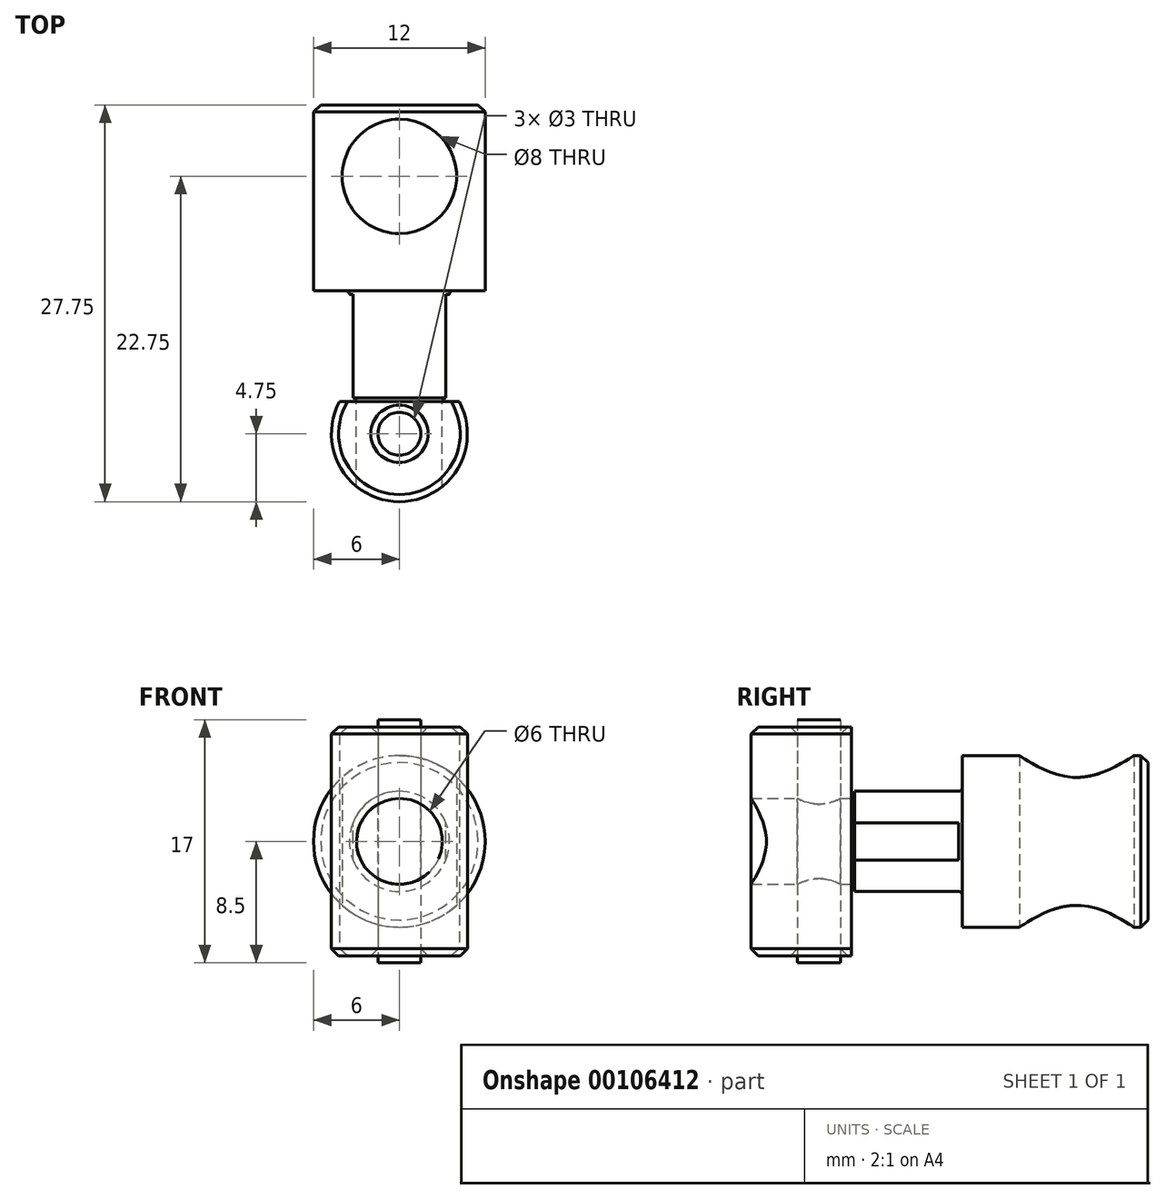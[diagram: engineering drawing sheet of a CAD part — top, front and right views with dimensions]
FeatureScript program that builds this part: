
annotation { "Feature Type Name" : "Feature", "Feature Type Description" : "" }
export const myFeature = defineFeature(function(context is Context, id is Id, definition is map)
    precondition{}
    {
        {
            var Q0;
            Q0=qCreatedBy(makeId("Top.planeOp"),FACE);
            var sketch = newSketch(context, id + "F0", { "sketchPlane" : qUnion([Q0])});
            skCircle(sketch, "E0", {"center": v(0, 0) * mm, "radius": 4.75 * mm});
            skLineSegment(sketch, "E1", {"start": v(-4.18, 2.25) * mm, "end": v(4.18, 2.25) * mm});
            skCircle(sketch, "E2", {"center": v(0, 0) * mm, "radius": 1.5 * mm});
            skSolve(sketch);
        }
        {
            var Q0;
            {var subQ0=sQuery(id+"F0.wireOp",EDGE,"E1");Q0=makeQuery(id+"F0.imprint","IMPRINT",FACE,{"disambiguationData":[TD([[makeQuery(id+"F0.imprint","IMPRINT",EDGE,{"derivedFrom":subQ0}),-1.0]])]});}
            extrude(context, id + "F1", {"entities" : qUnion([Q0]), "depth" : 16 * mm, "symmetric" : true});
        }
        {
            var Q0;
            Q0=makeQuery(id+"F1.opExtrude","CAP_EDGE",EDGE,{"disambiguationData":[OSD([sQuery(id+"F0.wireOp",EDGE,"E0")])],"isStart":false});
            var Q1;
            Q1=makeQuery(id+"F1.opExtrude","CAP_EDGE",EDGE,{"disambiguationData":[OSD([sQuery(id+"F0.wireOp",EDGE,"E0")])],"isStart":true});
            chamfer(context, id + "F2", {"entities" : qUnion([Q0, Q1]), "width" : 0.5 * mm, "tangentPropagation" : true});
        }
        {
            var Q0;
            Q0=makeQuery(id+"F1.opExtrude","SWEPT_FACE",FACE,{"disambiguationData":[OSD([sQuery(id+"F0.wireOp",EDGE,"E1")])]});
            var sketch = newSketch(context, id + "F3", { "sketchPlane" : qUnion([Q0])});
            skCircle(sketch, "E3", {"center": v(0, 0) * mm, "radius": 3 * mm});
            skSolve(sketch);
        }
        {
            var Q0;
            Q0=makeQuery(id+"F3.imprint","IMPRINT",FACE,{"disambiguationData":[TD([[makeQuery(id+"F3.imprint","IMPRINT",EDGE,{"derivedFrom":sQuery(id+"F3.wireOp",EDGE,"E3")}),1.0]])]});
            extrude(context, id + "F4", {"entities" : qUnion([Q0]), "operationType" : NewBodyOperationType.REMOVE, "endBound" : BoundingType.THROUGH_ALL, "oppositeDirection" : true, "depth" : 25 * mm});
        }
        {
            var Q0;
            Q0=qCreatedBy(makeId("Right.planeOp"),FACE);
            var sketch = newSketch(context, id + "F5", { "sketchPlane" : qUnion([Q0])});
            skLineSegment(sketch, "E4", {"start": v(-5, 0) * mm, "end": v(-5, 3) * mm});
            skLineSegment(sketch, "E5", {"start": v(-5, 3) * mm, "end": v(2.25, 3) * mm});
            skLineSegment(sketch, "E6", {"start": v(2.5, 3.25) * mm, "end": v(2.5, 3.5) * mm});
            skLineSegment(sketch, "E7", {"start": v(2.5, 3.5) * mm, "end": v(9.75, 3.5) * mm});
            skLineSegment(sketch, "E8", {"start": v(10, 3.75) * mm, "end": v(10, 6) * mm});
            skLineSegment(sketch, "E9", {"start": v(10, 6) * mm, "end": v(23, 6) * mm});
            skLineSegment(sketch, "E10", {"start": v(23, 6) * mm, "end": v(23, 0) * mm});
            skLineSegment(sketch, "E11", {"start": v(23, 0) * mm, "end": v(-5, 0) * mm});
            skPoint(sketch, "E12.visualSharp", {"position": v(2.5, 3) * mm});
            skArc(sketch, "E12.filletArc", {"start": v(2.25, 3) * mm, "mid": v(2.43, 3.07) * mm, "end": v(2.5, 3.25) * mm});
            skPoint(sketch, "E13.visualSharp", {"position": v(10, 3.5) * mm});
            skArc(sketch, "E13.filletArc", {"start": v(9.75, 3.5) * mm, "mid": v(9.93, 3.57) * mm, "end": v(10, 3.75) * mm});
            skSolve(sketch);
        }
        {
            var Q0;
            Q0=qSketchRegion(id+"F5",true);
            var Q1;
            Q1=sQuery(id+"F5.wireOp",EDGE,"E11");
            revolve(context, id + "F6", {"entities" : qUnion([Q0]), "axis" : qUnion([Q1]), "revolveType" : RevolveType.FULL});
        }
        {
            var Q0;
            Q0=qCreatedBy(makeId("Top.planeOp"),FACE);
            var sketch = newSketch(context, id + "F7", { "sketchPlane" : qUnion([Q0])});
            skLineSegment(sketch, "E14.bottom", {"start": v(-7.5, 9.75) * mm, "end": v(-3.25, 9.75) * mm});
            skLineSegment(sketch, "E14.top", {"start": v(-7.5, 2.5) * mm, "end": v(-3.25, 2.5) * mm});
            skLineSegment(sketch, "E14.left", {"start": v(-7.5, 9.75) * mm, "end": v(-7.5, 2.5) * mm});
            skLineSegment(sketch, "E14.right", {"start": v(-3.25, 9.75) * mm, "end": v(-3.25, 2.5) * mm});
            skLineSegment(sketch, "E15.bottom", {"start": v(7.5, 9.75) * mm, "end": v(3.25, 9.75) * mm});
            skLineSegment(sketch, "E15.top", {"start": v(7.5, 2.5) * mm, "end": v(3.25, 2.5) * mm});
            skLineSegment(sketch, "E15.left", {"start": v(7.5, 9.75) * mm, "end": v(7.5, 2.5) * mm});
            skLineSegment(sketch, "E15.right", {"start": v(3.25, 9.75) * mm, "end": v(3.25, 2.5) * mm});
            skSolve(sketch);
        }
        {
            var Q0;
            Q0=makeQuery(id+"F7.imprint","IMPRINT",FACE,{"disambiguationData":[TD([[makeQuery(id+"F7.imprint","IMPRINT",EDGE,{"derivedFrom":sQuery(id+"F7.wireOp",EDGE,"E14.bottom")}),-1.0]])]});
            var Q1;
            Q1=makeQuery(id+"F7.imprint","IMPRINT",FACE,{"disambiguationData":[TD([[makeQuery(id+"F7.imprint","IMPRINT",EDGE,{"derivedFrom":sQuery(id+"F7.wireOp",EDGE,"E15.bottom")}),1.0]])]});
            extrude(context, id + "F8", {"entities" : qUnion([Q0, Q1]), "operationType" : NewBodyOperationType.REMOVE, "oppositeDirection" : true, "depth" : 25 * mm, "symmetric" : true});
        }
        {
            var Q0;
            Q0=qCreatedBy(makeId("Top.planeOp"),FACE);
            var sketch = newSketch(context, id + "F9", { "sketchPlane" : qUnion([Q0])});
            skCircle(sketch, "E16", {"center": v(0, 0) * mm, "radius": 1.5 * mm});
            skSolve(sketch);
        }
        {
            var Q0;
            Q0=makeQuery(id+"F9.imprint","IMPRINT",FACE,{"disambiguationData":[TD([[makeQuery(id+"F9.imprint","IMPRINT",EDGE,{"derivedFrom":sQuery(id+"F9.wireOp",EDGE,"E16")}),1.0]])]});
            extrude(context, id + "F10", {"entities" : qUnion([Q0]), "operationType" : NewBodyOperationType.REMOVE, "oppositeDirection" : true, "depth" : 25 * mm, "symmetric" : true});
        }
        {
            var Q0;
            Q0=qCreatedBy(makeId("Top.planeOp"),FACE);
            var sketch = newSketch(context, id + "F11", { "sketchPlane" : qUnion([Q0])});
            skArc(sketch, "E17", {"start": v(-3, -3.68) * mm, "mid": v(0, -4.75) * mm, "end": v(3, -3.68) * mm});
            skLineSegment(sketch, "E18", {"start": v(-3, -3.68) * mm, "end": v(-3, -5.68) * mm});
            skLineSegment(sketch, "E19", {"start": v(-3, -5.68) * mm, "end": v(3, -5.68) * mm});
            skLineSegment(sketch, "E20", {"start": v(3, -5.68) * mm, "end": v(3, -3.68) * mm});
            skSolve(sketch);
        }
        {
            var Q0;
            Q0=makeQuery(id+"F11.imprint","IMPRINT",FACE,{"disambiguationData":[TD([[makeQuery(id+"F11.imprint","IMPRINT",EDGE,{"derivedFrom":sQuery(id+"F11.wireOp",EDGE,"E17")}),-1.0]])]});
            extrude(context, id + "F12", {"entities" : qUnion([Q0]), "operationType" : NewBodyOperationType.REMOVE, "oppositeDirection" : true, "depth" : 25 * mm, "symmetric" : true});
        }
        {
            var Q0;
            Q0=qCreatedBy(makeId("Top.planeOp"),FACE);
            var sketch = newSketch(context, id + "F13", { "sketchPlane" : qUnion([Q0])});
            skCircle(sketch, "E21", {"center": v(0, 18) * mm, "radius": 4 * mm});
            skSolve(sketch);
        }
        {
            var Q0;
            Q0=qSketchRegion(id+"F13",true);
            extrude(context, id + "F14", {"entities" : qUnion([Q0]), "operationType" : NewBodyOperationType.REMOVE, "depth" : 25 * mm, "symmetric" : true});
        }
        {
            var Q0;
            Q0=makeQuery(id+"F6.opRevolve","SWEPT_EDGE",EDGE,{"disambiguationData":[OSD([sQuery(id+"F5.wireOp",EDGE,"E9"),sQuery(id+"F5.wireOp",EDGE,"E10")])]});
            chamfer(context, id + "F15", {"entities" : qUnion([Q0]), "width" : 0.5 * mm, "tangentPropagation" : true});
        }
        {
            var Q0;
            Q0=qCreatedBy(makeId("Top.planeOp"),FACE);
            var sketch = newSketch(context, id + "F16", { "sketchPlane" : qUnion([Q0])});
            skCircle(sketch, "E22", {"center": v(0, 0) * mm, "radius": 1.5 * mm});
            skSolve(sketch);
        }
        {
            var Q0;
            Q0=makeQuery(id+"F16.imprint","IMPRINT",FACE,{"disambiguationData":[TD([[makeQuery(id+"F16.imprint","IMPRINT",EDGE,{"derivedFrom":sQuery(id+"F16.wireOp",EDGE,"E22")}),1.0]])]});
            extrude(context, id + "F17", {"entities" : qUnion([Q0]), "depth" : 17 * mm, "symmetric" : true});
        }
        {
            var Q0;
            Q0=makeQuery(id+"F1.opExtrude","CAP_EDGE",EDGE,{"disambiguationData":[OSD([sQuery(id+"F0.wireOp",EDGE,"E2")])],"isStart":false});
            var Q1;
            Q1=makeQuery(id+"F1.opExtrude","CAP_EDGE",EDGE,{"disambiguationData":[OSD([sQuery(id+"F0.wireOp",EDGE,"E2")])],"isStart":true});
            chamfer(context, id + "F18", {"entities" : qUnion([Q0, Q1]), "width" : 0.5 * mm, "tangentPropagation" : true});
        }
    });
